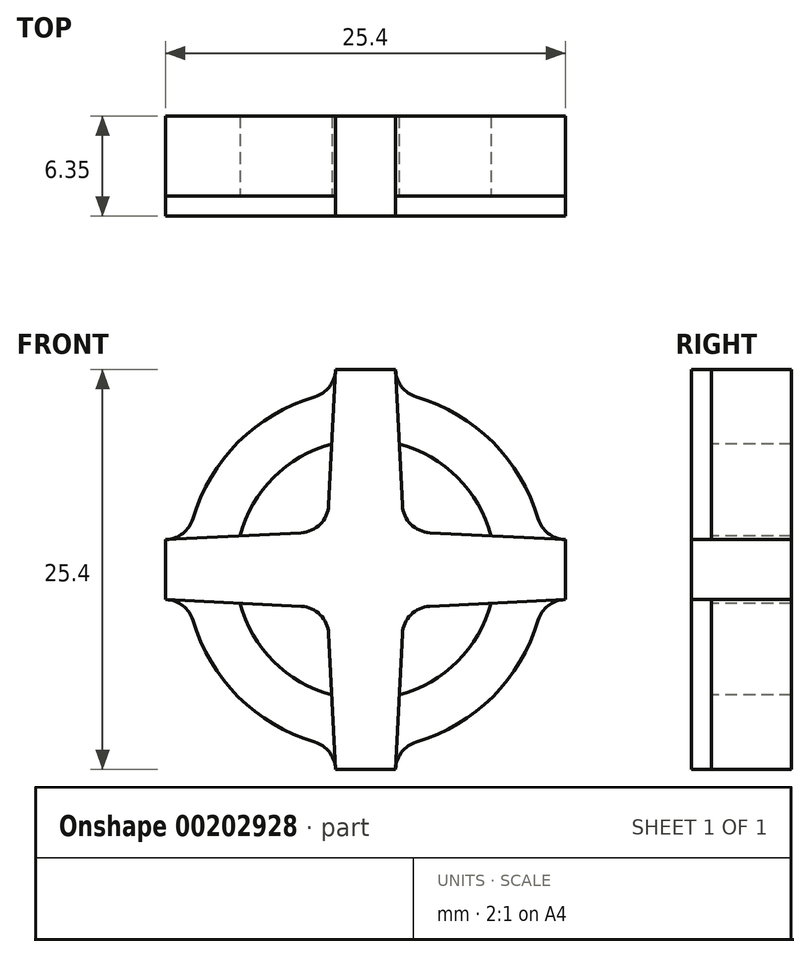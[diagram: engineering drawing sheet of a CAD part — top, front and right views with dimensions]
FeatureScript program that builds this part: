
annotation { "Feature Type Name" : "Feature", "Feature Type Description" : "" }
export const myFeature = defineFeature(function(context is Context, id is Id, definition is map)
    precondition{}
    {
        {
            var Q0;
            Q0=qCreatedBy(makeId("Front.planeOp"),FACE);
            var sketch = newSketch(context, id + "F0", { "sketchPlane" : qUnion([Q0])});
            skCircle(sketch, "E0", {"center": v(0, 0) * mm, "radius": 11.43 * mm});
            skLineSegment(sketch, "E1.bottom", {"start": v(-2.7, 0) * mm, "end": v(2.7, 0) * mm});
            skLineSegment(sketch, "E1.top", {"start": v(-1.9, 19.5) * mm, "end": v(1.9, 19.5) * mm});
            skPoint(sketch, "E2", {"position": v(0, 19.5) * mm});
            skSolve(sketch);
        }
        {
            var Q0;
            Q0 = qSketchRegion(id + "F0", true);
            var Q1;
            Q1 = qSketchRegion(id + "F2", true);
            extrude(context, id + "F1", {"entities" : qUnion([Q0, Q1]), "depth" : 5.08 * mm});
        }
        {
            var Q0;
            Q0=makeQuery(id+"F1.opExtrude","CAP_FACE",FACE,{"disambiguationData":[OSD([sQuery(id+"F0.wireOp",EDGE,"E0")])],"isStart":false});
            var sketch = newSketch(context, id + "F2", { "sketchPlane" : qUnion([Q0])});
            skCircle(sketch, "E3", {"center": v(0, 0) * mm, "radius": 9.53 * mm});
            skSolve(sketch);
        }
        {
            var Q0;
            Q0=sQuery(id+"F2.wireOp",VERTEX,"E3.center");
            var Q1;
            Q1=makeQuery(id+"F1.opExtrude","SWEPT_BODY",BODY,{"disambiguationData":[OSD([sQuery(id+"F0.wireOp",EDGE,"E0")])]});
            hole(context, id + "F3", {"style" : HoleStyle.SIMPLE, "endStyle" : HoleEndStyle.THROUGH, "holeDiameter" : 16.5 * mm, "locations" : qUnion([Q0]), "scope" : qUnion([Q1]), "isTappedThrough" : true});
        }
        {
            var Q0;
            Q0=qCreatedBy(makeId("Front.planeOp"),FACE);
            var sketch = newSketch(context, id + "F4", { "sketchPlane" : qUnion([Q0])});
            skLineSegment(sketch, "E4.bottom", {"start": v(-2.54, 0) * mm, "end": v(2.54, 0) * mm});
            skLineSegment(sketch, "E4.top", {"start": v(-1.9, 12.7) * mm, "end": v(1.9, 12.7) * mm});
            skPoint(sketch, "E5", {"position": v(0, 12.7) * mm});
            skLineSegment(sketch, "E6", {"start": v(-2.54, 0) * mm, "end": v(-1.9, 12.7) * mm});
            skLineSegment(sketch, "E7", {"start": v(2.54, 0) * mm, "end": v(1.9, 12.7) * mm});
            skLineSegment(sketch, "E8.MirrorCS", {"start": v(-1.9, -12.7) * mm, "end": v(1.9, -12.7) * mm});
            skLineSegment(sketch, "E9.MirrorCS", {"start": v(-2.54, 0) * mm, "end": v(-1.9, -12.7) * mm});
            skLineSegment(sketch, "E10.MirrorCS", {"start": v(2.54, 0) * mm, "end": v(1.9, -12.7) * mm});
            skLineSegment(sketch, "E11", {"start": v(-31.34, 31.34) * mm, "end": v(31.34, -31.34) * mm, "construction": true});
            skLineSegment(sketch, "E12.MirrorCS", {"start": v(12.7, 1.9) * mm, "end": v(12.7, -1.9) * mm});
            skLineSegment(sketch, "E13.MirrorCS", {"start": v(0, -2.54) * mm, "end": v(12.7, -1.9) * mm});
            skLineSegment(sketch, "E14.MirrorCS", {"start": v(0, 2.54) * mm, "end": v(12.7, 1.9) * mm});
            skLineSegment(sketch, "E15.MirrorCS", {"start": v(-12.7, 1.9) * mm, "end": v(-12.7, -1.9) * mm});
            skLineSegment(sketch, "E16.MirrorCS", {"start": v(0, 2.54) * mm, "end": v(-12.7, 1.9) * mm});
            skLineSegment(sketch, "E17.MirrorCS", {"start": v(0, 2.54) * mm, "end": v(0, -2.54) * mm});
            skPoint(sketch, "E18.MirrorP", {"position": v(-12.7, 0) * mm});
            skLineSegment(sketch, "E19.MirrorCS", {"start": v(0, -2.54) * mm, "end": v(-12.7, -1.9) * mm});
            skSolve(sketch);
        }
        {
            var Q0;
            {var subQ0=sQuery(id+"F4.wireOp",EDGE,"E15.MirrorCS");Q0=makeQuery(id+"F4.imprint","IMPRINT",FACE,{"disambiguationData":[TD([[makeQuery(id+"F4.imprint","IMPRINT",EDGE,{"derivedFrom":subQ0}),1.0]])]});}
            var Q1;
            {var subQ5=sQuery(id+"F4.wireOp",EDGE,"E8.MirrorCS");Q1=makeQuery(id+"F4.imprint","IMPRINT",FACE,{"disambiguationData":[TD([[makeQuery(id+"F4.imprint","IMPRINT",EDGE,{"derivedFrom":subQ5}),1.0]])]});}
            var Q2;
            {var subQ1=sQuery(id+"F4.wireOp",EDGE,"E12.MirrorCS");Q2=makeQuery(id+"F4.imprint","IMPRINT",FACE,{"disambiguationData":[TD([[makeQuery(id+"F4.imprint","IMPRINT",EDGE,{"derivedFrom":subQ1}),-1.0]])]});}
            var Q3;
            {var subQ1=sQuery(id+"F4.wireOp",EDGE,"E4.top");Q3=makeQuery(id+"F4.imprint","IMPRINT",FACE,{"disambiguationData":[TD([[makeQuery(id+"F4.imprint","IMPRINT",EDGE,{"derivedFrom":subQ1}),-1.0]])]});}
            var Q4;
            {var subQ0=sQuery(id+"F4.wireOp",EDGE,"E9.MirrorCS");var subQ5=sQuery(id+"F4.wireOp",EDGE,"E19.MirrorCS");var subQ6=makeQuery(id+"F4.imprint","INTERSECT",VERTEX,{"derivedFrom":[subQ0,subQ5]});Q4=makeQuery(id+"F4.imprint","IMPRINT",FACE,{"disambiguationData":[TD([[makeQuery(id+"F4.imprint","IMPRINT",EDGE,{"disambiguationData":[TD([[subQ6,1.0]])],"derivedFrom":subQ0}),1.0]])]});}
            var Q5;
            {var subQ1=sQuery(id+"F4.wireOp",EDGE,"E7");var subQ3=sQuery(id+"F4.wireOp",EDGE,"E14.MirrorCS");var subQ4=makeQuery(id+"F4.imprint","INTERSECT",VERTEX,{"derivedFrom":[subQ1,subQ3]});Q5=makeQuery(id+"F4.imprint","IMPRINT",FACE,{"disambiguationData":[TD([[makeQuery(id+"F4.imprint","IMPRINT",EDGE,{"disambiguationData":[TD([[subQ4,1.0]])],"derivedFrom":subQ1}),1.0]])]});}
            var Q6;
            {var subQ0=sQuery(id+"F4.wireOp",EDGE,"E16.MirrorCS");var subQ1=sQuery(id+"F4.wireOp",EDGE,"E11");var subQ2=makeQuery(id+"F4.imprint","INTERSECT",VERTEX,{"derivedFrom":[sQuery(id+"F4.wireOp",EDGE,"E6"),subQ1,subQ0]});Q6=makeQuery(id+"F4.imprint","IMPRINT",FACE,{"disambiguationData":[TD([[makeQuery(id+"F4.imprint","IMPRINT",EDGE,{"disambiguationData":[TD([[subQ2,-1.0]])],"derivedFrom":subQ1}),1.0]])]});}
            var Q7;
            {var subQ0=sQuery(id+"F4.wireOp",EDGE,"E4.bottom");var subQ1=sQuery(id+"F4.wireOp",EDGE,"E6");var subQ2=makeQuery(id+"F4.imprint","INTERSECT",VERTEX,{"derivedFrom":[subQ1,subQ0,sQuery(id+"F4.wireOp",EDGE,"E9.MirrorCS")]});Q7=makeQuery(id+"F4.imprint","IMPRINT",FACE,{"disambiguationData":[TD([[makeQuery(id+"F4.imprint","IMPRINT",EDGE,{"disambiguationData":[TD([[subQ2,-1.0]])],"derivedFrom":subQ1}),-1.0]])]});}
            var Q8;
            {var subQ0=sQuery(id+"F4.wireOp",EDGE,"E13.MirrorCS");var subQ1=sQuery(id+"F4.wireOp",EDGE,"E11");var subQ2=makeQuery(id+"F4.imprint","INTERSECT",VERTEX,{"derivedFrom":[sQuery(id+"F4.wireOp",EDGE,"E10.MirrorCS"),subQ1,subQ0]});Q8=makeQuery(id+"F4.imprint","IMPRINT",FACE,{"disambiguationData":[TD([[makeQuery(id+"F4.imprint","IMPRINT",EDGE,{"disambiguationData":[TD([[subQ2,1.0]])],"derivedFrom":subQ1}),-1.0]])]});}
            var Q9;
            {var subQ0=sQuery(id+"F4.wireOp",EDGE,"E10.MirrorCS");var subQ1=sQuery(id+"F4.wireOp",EDGE,"E4.bottom");var subQ2=makeQuery(id+"F4.imprint","INTERSECT",VERTEX,{"derivedFrom":[sQuery(id+"F4.wireOp",EDGE,"E7"),subQ1,subQ0]});Q9=makeQuery(id+"F4.imprint","IMPRINT",FACE,{"disambiguationData":[TD([[makeQuery(id+"F4.imprint","IMPRINT",EDGE,{"disambiguationData":[TD([[subQ2,1.0]])],"derivedFrom":subQ1}),-1.0]])]});}
            extrude(context, id + "F5", {"entities" : qUnion([Q0, Q1, Q2, Q3, Q4, Q5, Q6, Q7, Q8, Q9]), "operationType" : NewBodyOperationType.ADD, "depth" : 6.35 * mm});
        }
        {
            var Q0;
            Q0=makeQuery(id+"F5.boolean.opBoolean","INTERSECT",EDGE,{"derivedFrom":[makeQuery(id+"F3.hole-0.boolean.opBoolean","COPY",FACE,{"derivedFrom":makeQuery(id+"F3.hole-0.opRevolve","SWEPT_FACE",FACE,{"disambiguationData":[OSD([sQuery(id+"F3.hole-0.sketch.wireOp",EDGE,"core_line_2")])]})}),makeQuery(id+"F5.opExtrude","SWEPT_FACE",FACE,{"disambiguationData":[OSD([sQuery(id+"F4.wireOp",EDGE,"E19.MirrorCS")])]})]});
            var Q1;
            Q1=makeQuery(id+"F5.boolean.opBoolean","INTERSECT",EDGE,{"derivedFrom":[makeQuery(id+"F3.hole-0.boolean.opBoolean","COPY",FACE,{"derivedFrom":makeQuery(id+"F3.hole-0.opRevolve","SWEPT_FACE",FACE,{"disambiguationData":[OSD([sQuery(id+"F3.hole-0.sketch.wireOp",EDGE,"core_line_2")])]})}),makeQuery(id+"F5.opExtrude","SWEPT_FACE",FACE,{"disambiguationData":[OSD([sQuery(id+"F4.wireOp",EDGE,"E9.MirrorCS")])]})]});
            var Q2;
            Q2=makeQuery(id+"F5.opExtrude","SWEPT_EDGE",EDGE,{"disambiguationData":[OSD([sQuery(id+"F4.wireOp",EDGE,"E9.MirrorCS"),sQuery(id+"F4.wireOp",EDGE,"E19.MirrorCS")])]});
            var Q3;
            Q3=makeQuery(id+"F5.boolean.opBoolean","INTERSECT",EDGE,{"derivedFrom":[makeQuery(id+"F3.hole-0.boolean.opBoolean","COPY",FACE,{"derivedFrom":makeQuery(id+"F3.hole-0.opRevolve","SWEPT_FACE",FACE,{"disambiguationData":[OSD([sQuery(id+"F3.hole-0.sketch.wireOp",EDGE,"core_line_2")])]})}),makeQuery(id+"F5.opExtrude","SWEPT_FACE",FACE,{"disambiguationData":[OSD([sQuery(id+"F4.wireOp",EDGE,"E6")])]})]});
            var Q4;
            Q4=makeQuery(id+"F5.boolean.opBoolean","INTERSECT",EDGE,{"derivedFrom":[makeQuery(id+"F3.hole-0.boolean.opBoolean","COPY",FACE,{"derivedFrom":makeQuery(id+"F3.hole-0.opRevolve","SWEPT_FACE",FACE,{"disambiguationData":[OSD([sQuery(id+"F3.hole-0.sketch.wireOp",EDGE,"core_line_2")])]})}),makeQuery(id+"F5.opExtrude","SWEPT_FACE",FACE,{"disambiguationData":[OSD([sQuery(id+"F4.wireOp",EDGE,"E16.MirrorCS")])]})]});
            var Q5;
            Q5=makeQuery(id+"F5.opExtrude","SWEPT_EDGE",EDGE,{"disambiguationData":[OSD([sQuery(id+"F4.wireOp",EDGE,"E6"),sQuery(id+"F4.wireOp",EDGE,"E11"),sQuery(id+"F4.wireOp",EDGE,"E16.MirrorCS")])]});
            var Q6;
            Q6=makeQuery(id+"F5.opExtrude","SWEPT_EDGE",EDGE,{"disambiguationData":[OSD([sQuery(id+"F4.wireOp",EDGE,"E7"),sQuery(id+"F4.wireOp",EDGE,"E14.MirrorCS")])]});
            var Q7;
            Q7=makeQuery(id+"F5.boolean.opBoolean","INTERSECT",EDGE,{"derivedFrom":[makeQuery(id+"F3.hole-0.boolean.opBoolean","COPY",FACE,{"derivedFrom":makeQuery(id+"F3.hole-0.opRevolve","SWEPT_FACE",FACE,{"disambiguationData":[OSD([sQuery(id+"F3.hole-0.sketch.wireOp",EDGE,"core_line_2")])]})}),makeQuery(id+"F5.opExtrude","SWEPT_FACE",FACE,{"disambiguationData":[OSD([sQuery(id+"F4.wireOp",EDGE,"E7")])]})]});
            var Q8;
            Q8=makeQuery(id+"F5.opExtrude","SWEPT_EDGE",EDGE,{"disambiguationData":[OSD([sQuery(id+"F4.wireOp",EDGE,"E10.MirrorCS"),sQuery(id+"F4.wireOp",EDGE,"E11"),sQuery(id+"F4.wireOp",EDGE,"E13.MirrorCS")])]});
            var Q9;
            Q9=makeQuery(id+"F5.boolean.opBoolean","INTERSECT",EDGE,{"derivedFrom":[makeQuery(id+"F3.hole-0.boolean.opBoolean","COPY",FACE,{"derivedFrom":makeQuery(id+"F3.hole-0.opRevolve","SWEPT_FACE",FACE,{"disambiguationData":[OSD([sQuery(id+"F3.hole-0.sketch.wireOp",EDGE,"core_line_2")])]})}),makeQuery(id+"F5.opExtrude","SWEPT_FACE",FACE,{"disambiguationData":[OSD([sQuery(id+"F4.wireOp",EDGE,"E13.MirrorCS")])]})]});
            var Q10;
            Q10=makeQuery(id+"F5.boolean.opBoolean","INTERSECT",EDGE,{"derivedFrom":[makeQuery(id+"F3.hole-0.boolean.opBoolean","COPY",FACE,{"derivedFrom":makeQuery(id+"F3.hole-0.opRevolve","SWEPT_FACE",FACE,{"disambiguationData":[OSD([sQuery(id+"F3.hole-0.sketch.wireOp",EDGE,"core_line_2")])]})}),makeQuery(id+"F5.opExtrude","SWEPT_FACE",FACE,{"disambiguationData":[OSD([sQuery(id+"F4.wireOp",EDGE,"E14.MirrorCS")])]})]});
            var Q11;
            Q11=makeQuery(id+"F5.boolean.opBoolean","INTERSECT",EDGE,{"derivedFrom":[makeQuery(id+"F3.hole-0.boolean.opBoolean","COPY",FACE,{"derivedFrom":makeQuery(id+"F3.hole-0.opRevolve","SWEPT_FACE",FACE,{"disambiguationData":[OSD([sQuery(id+"F3.hole-0.sketch.wireOp",EDGE,"core_line_2")])]})}),makeQuery(id+"F5.opExtrude","SWEPT_FACE",FACE,{"disambiguationData":[OSD([sQuery(id+"F4.wireOp",EDGE,"E10.MirrorCS")])]})]});
            var Q12;
            Q12=makeQuery(id+"F5.boolean.opBoolean","INTERSECT",EDGE,{"derivedFrom":[makeQuery(id+"F1.opExtrude","SWEPT_FACE",FACE,{"disambiguationData":[OSD([sQuery(id+"F0.wireOp",EDGE,"E0")])]}),makeQuery(id+"F5.opExtrude","SWEPT_FACE",FACE,{"disambiguationData":[OSD([sQuery(id+"F4.wireOp",EDGE,"E19.MirrorCS")])]})]});
            var Q13;
            Q13=makeQuery(id+"F5.boolean.opBoolean","INTERSECT",EDGE,{"derivedFrom":[makeQuery(id+"F1.opExtrude","SWEPT_FACE",FACE,{"disambiguationData":[OSD([sQuery(id+"F0.wireOp",EDGE,"E0")])]}),makeQuery(id+"F5.opExtrude","SWEPT_FACE",FACE,{"disambiguationData":[OSD([sQuery(id+"F4.wireOp",EDGE,"E9.MirrorCS")])]})]});
            var Q14;
            Q14=makeQuery(id+"F5.boolean.opBoolean","INTERSECT",EDGE,{"derivedFrom":[makeQuery(id+"F1.opExtrude","SWEPT_FACE",FACE,{"disambiguationData":[OSD([sQuery(id+"F0.wireOp",EDGE,"E0")])]}),makeQuery(id+"F5.opExtrude","SWEPT_FACE",FACE,{"disambiguationData":[OSD([sQuery(id+"F4.wireOp",EDGE,"E10.MirrorCS")])]})]});
            var Q15;
            Q15=makeQuery(id+"F5.boolean.opBoolean","INTERSECT",EDGE,{"derivedFrom":[makeQuery(id+"F1.opExtrude","SWEPT_FACE",FACE,{"disambiguationData":[OSD([sQuery(id+"F0.wireOp",EDGE,"E0")])]}),makeQuery(id+"F5.opExtrude","SWEPT_FACE",FACE,{"disambiguationData":[OSD([sQuery(id+"F4.wireOp",EDGE,"E13.MirrorCS")])]})]});
            var Q16;
            Q16=makeQuery(id+"F5.boolean.opBoolean","INTERSECT",EDGE,{"derivedFrom":[makeQuery(id+"F1.opExtrude","SWEPT_FACE",FACE,{"disambiguationData":[OSD([sQuery(id+"F0.wireOp",EDGE,"E0")])]}),makeQuery(id+"F5.opExtrude","SWEPT_FACE",FACE,{"disambiguationData":[OSD([sQuery(id+"F4.wireOp",EDGE,"E14.MirrorCS")])]})]});
            var Q17;
            Q17=makeQuery(id+"F5.boolean.opBoolean","INTERSECT",EDGE,{"derivedFrom":[makeQuery(id+"F1.opExtrude","SWEPT_FACE",FACE,{"disambiguationData":[OSD([sQuery(id+"F0.wireOp",EDGE,"E0")])]}),makeQuery(id+"F5.opExtrude","SWEPT_FACE",FACE,{"disambiguationData":[OSD([sQuery(id+"F4.wireOp",EDGE,"E7")])]})]});
            var Q18;
            Q18=makeQuery(id+"F5.boolean.opBoolean","INTERSECT",EDGE,{"derivedFrom":[makeQuery(id+"F1.opExtrude","SWEPT_FACE",FACE,{"disambiguationData":[OSD([sQuery(id+"F0.wireOp",EDGE,"E0")])]}),makeQuery(id+"F5.opExtrude","SWEPT_FACE",FACE,{"disambiguationData":[OSD([sQuery(id+"F4.wireOp",EDGE,"E6")])]})]});
            var Q19;
            Q19=makeQuery(id+"F5.boolean.opBoolean","INTERSECT",EDGE,{"derivedFrom":[makeQuery(id+"F1.opExtrude","SWEPT_FACE",FACE,{"disambiguationData":[OSD([sQuery(id+"F0.wireOp",EDGE,"E0")])]}),makeQuery(id+"F5.opExtrude","SWEPT_FACE",FACE,{"disambiguationData":[OSD([sQuery(id+"F4.wireOp",EDGE,"E16.MirrorCS")])]})]});
            fillet(context, id + "F6", {"entities" : qUnion([Q0, Q1, Q2, Q3, Q4, Q5, Q6, Q7, Q8, Q9, Q10, Q11, Q12, Q13, Q14, Q15, Q16, Q17, Q18, Q19]), "radius" : 1.84 * mm, "tangentPropagation" : true, "allowEdgeOverflow" : false});
        }
    });
